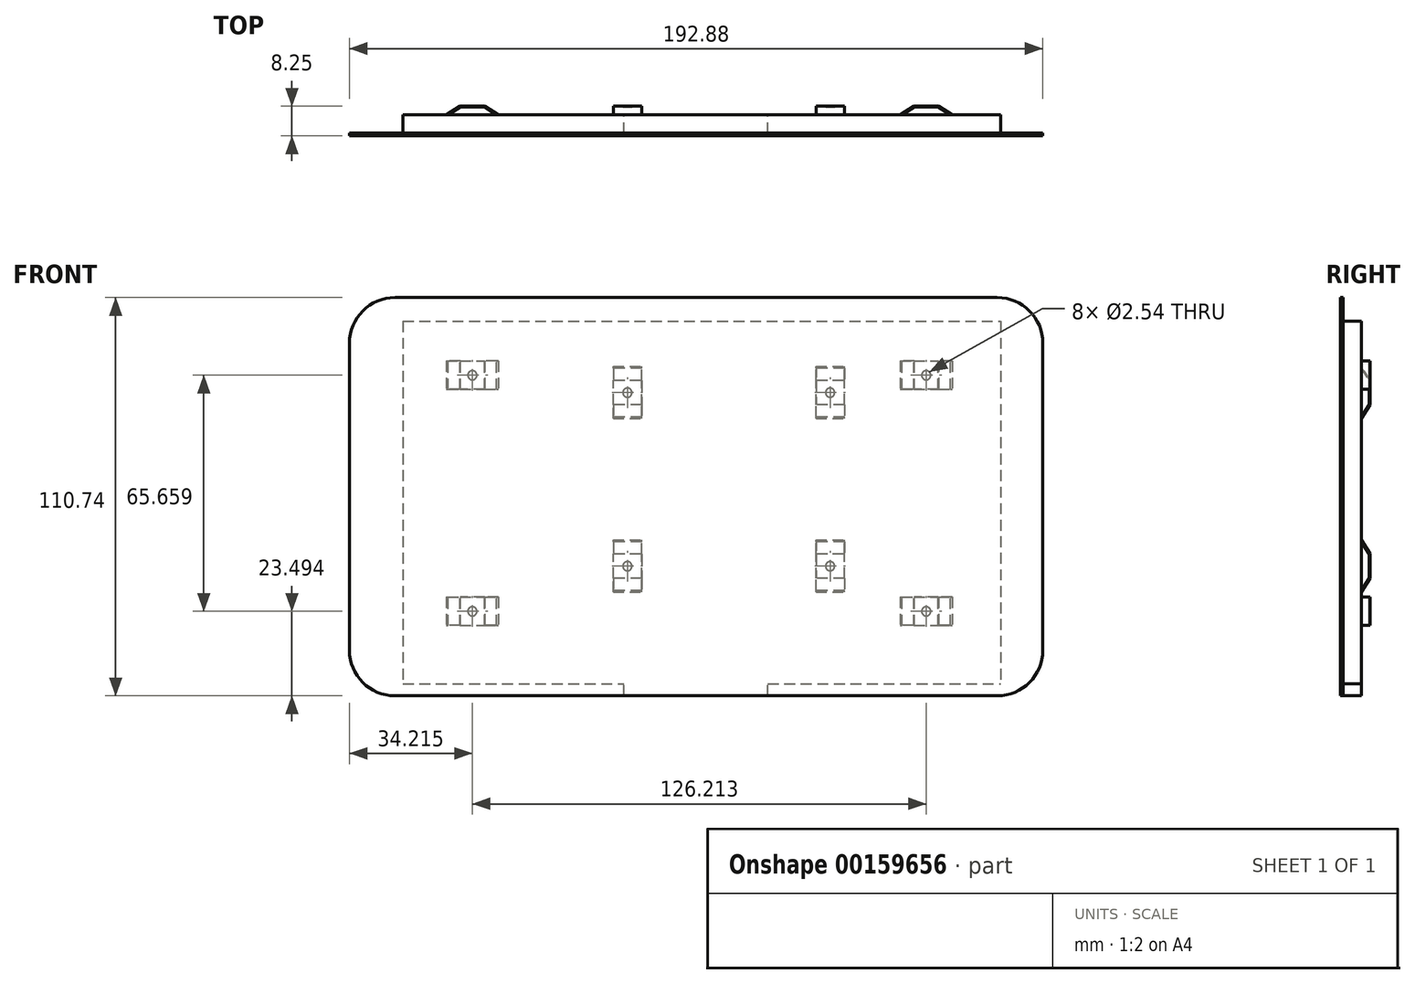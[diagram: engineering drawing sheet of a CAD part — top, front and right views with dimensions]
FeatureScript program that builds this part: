
annotation { "Feature Type Name" : "Feature", "Feature Type Description" : "" }
export const myFeature = defineFeature(function(context is Context, id is Id, definition is map)
    precondition{}
    {
        {
            var Q0;
            Q0=qCreatedBy(makeId("Front.planeOp"),FACE);
            var sketch = newSketch(context, id + "F0", { "sketchPlane" : qUnion([Q0])});
            skLineSegment(sketch, "E0.bottom", {"start": v(83.74, 55.37) * mm, "end": v(-83.74, 55.37) * mm});
            skLineSegment(sketch, "E0.top", {"start": v(83.74, -55.37) * mm, "end": v(-83.74, -55.37) * mm});
            skLineSegment(sketch, "E0.left", {"start": v(96.44, 42.67) * mm, "end": v(96.44, -42.67) * mm});
            skLineSegment(sketch, "E0.right", {"start": v(-96.44, 42.67) * mm, "end": v(-96.44, -42.67) * mm});
            skPoint(sketch, "E0.middle", {"position": v(0, 0) * mm});
            skPoint(sketch, "E1.visualSharp", {"position": v(-96.44, 55.37) * mm});
            skArc(sketch, "E1.filletArc", {"start": v(-83.74, 55.37) * mm, "mid": v(-92.72, 51.65) * mm, "end": v(-96.44, 42.67) * mm});
            skPoint(sketch, "E2.visualSharp", {"position": v(-96.44, -55.37) * mm});
            skArc(sketch, "E2.filletArc", {"start": v(-96.44, -42.67) * mm, "mid": v(-92.72, -51.65) * mm, "end": v(-83.74, -55.37) * mm});
            skPoint(sketch, "E3.visualSharp", {"position": v(96.44, -55.37) * mm});
            skArc(sketch, "E3.filletArc", {"start": v(83.74, -55.37) * mm, "mid": v(92.72, -51.65) * mm, "end": v(96.44, -42.67) * mm});
            skPoint(sketch, "E4.visualSharp", {"position": v(96.44, 55.37) * mm});
            skArc(sketch, "E4.filletArc", {"start": v(96.44, 42.67) * mm, "mid": v(92.72, 51.65) * mm, "end": v(83.74, 55.37) * mm});
            skSolve(sketch);
        }
        {
            var Q0;
            Q0 = qSketchRegion(id + "F0", true);
            extrude(context, id + "F1", {"entities" : qUnion([Q0]), "depth" : 0.76 * mm});
        }
        {
            var Q0;
            Q0=makeQuery(id+"F1.opExtrude","CAP_FACE",FACE,{"disambiguationData":[OSD([sQuery(id+"F0.wireOp",EDGE,"E0.bottom"),sQuery(id+"F0.wireOp",EDGE,"E0.top"),sQuery(id+"F0.wireOp",EDGE,"E0.left"),sQuery(id+"F0.wireOp",EDGE,"E0.right"),sQuery(id+"F0.wireOp",EDGE,"E1.filletArc"),sQuery(id+"F0.wireOp",EDGE,"E2.filletArc"),sQuery(id+"F0.wireOp",EDGE,"E3.filletArc"),sQuery(id+"F0.wireOp",EDGE,"E4.filletArc")])],"isStart":true});
            var sketch = newSketch(context, id + "F2", { "sketchPlane" : qUnion([Q0])});
            skLineSegment(sketch, "E5.bottom", {"start": v(81.54, 48.77) * mm, "end": v(-84.75, 48.77) * mm});
            skLineSegment(sketch, "E5.top", {"start": v(81.54, -52.03) * mm, "end": v(-84.75, -52.03) * mm});
            skLineSegment(sketch, "E5.left", {"start": v(81.54, 48.77) * mm, "end": v(81.54, -52.03) * mm});
            skLineSegment(sketch, "E5.right", {"start": v(-84.75, 48.77) * mm, "end": v(-84.75, -52.03) * mm});
            skPoint(sketch, "E5.middle", {"position": v(-1.6, -1.63) * mm});
            skSolve(sketch);
        }
        {
            var Q0;
            Q0 = qSketchRegion(id + "F2", true);
            extrude(context, id + "F3", {"entities" : qUnion([Q0]), "operationType" : NewBodyOperationType.ADD, "depth" : 5.08 * mm});
        }
        {
            var Q0;
            Q0=makeQuery(id+"F3.opExtrude","CAP_FACE",FACE,{"disambiguationData":[OSD([sQuery(id+"F2.wireOp",EDGE,"E5.bottom"),sQuery(id+"F2.wireOp",EDGE,"E5.top"),sQuery(id+"F2.wireOp",EDGE,"E5.left"),sQuery(id+"F2.wireOp",EDGE,"E5.right")])],"isStart":false});
            var sketch = newSketch(context, id + "F4", { "sketchPlane" : qUnion([Q0])});
            skLineSegment(sketch, "E6.bottom", {"start": v(-56.75, 37.72) * mm, "end": v(-71.23, 37.72) * mm});
            skLineSegment(sketch, "E6.top", {"start": v(-56.75, 29.85) * mm, "end": v(-71.23, 29.85) * mm});
            skLineSegment(sketch, "E6.left", {"start": v(-56.75, 37.72) * mm, "end": v(-56.75, 29.85) * mm});
            skLineSegment(sketch, "E6.right", {"start": v(-71.23, 37.72) * mm, "end": v(-71.23, 29.85) * mm});
            skPoint(sketch, "E6.middle", {"position": v(-63.99, 33.78) * mm});
            skLineSegment(sketch, "E7.bottom", {"start": v(-56.75, -27.94) * mm, "end": v(-71.23, -27.94) * mm});
            skLineSegment(sketch, "E7.top", {"start": v(-56.75, -35.81) * mm, "end": v(-71.23, -35.81) * mm});
            skLineSegment(sketch, "E7.left", {"start": v(-56.75, -27.94) * mm, "end": v(-56.75, -35.81) * mm});
            skLineSegment(sketch, "E7.right", {"start": v(-71.23, -27.94) * mm, "end": v(-71.23, -35.81) * mm});
            skPoint(sketch, "E7.middle", {"position": v(-63.99, -31.88) * mm});
            skLineSegment(sketch, "E8.bottom", {"start": v(69.46, 37.72) * mm, "end": v(54.99, 37.72) * mm});
            skLineSegment(sketch, "E8.top", {"start": v(69.46, 29.85) * mm, "end": v(54.99, 29.85) * mm});
            skLineSegment(sketch, "E8.left", {"start": v(69.46, 37.72) * mm, "end": v(69.46, 29.85) * mm});
            skLineSegment(sketch, "E8.right", {"start": v(54.99, 37.72) * mm, "end": v(54.99, 29.85) * mm});
            skPoint(sketch, "E8.middle", {"position": v(62.22, 33.78) * mm});
            skLineSegment(sketch, "E9.bottom", {"start": v(69.46, -27.94) * mm, "end": v(54.99, -27.94) * mm});
            skLineSegment(sketch, "E9.top", {"start": v(69.46, -35.81) * mm, "end": v(54.99, -35.81) * mm});
            skLineSegment(sketch, "E9.left", {"start": v(69.46, -27.94) * mm, "end": v(69.46, -35.81) * mm});
            skLineSegment(sketch, "E9.right", {"start": v(54.99, -27.94) * mm, "end": v(54.99, -35.81) * mm});
            skPoint(sketch, "E9.middle", {"position": v(62.22, -31.88) * mm});
            skLineSegment(sketch, "E10.bottom", {"start": v(-33.33, 21.72) * mm, "end": v(-41.2, 21.72) * mm});
            skLineSegment(sketch, "E10.top", {"start": v(-33.33, 36.2) * mm, "end": v(-41.2, 36.2) * mm});
            skLineSegment(sketch, "E10.left", {"start": v(-33.33, 21.72) * mm, "end": v(-33.33, 36.2) * mm});
            skLineSegment(sketch, "E10.right", {"start": v(-41.2, 21.72) * mm, "end": v(-41.2, 36.2) * mm});
            skPoint(sketch, "E10.middle", {"position": v(-37.27, 28.95) * mm});
            skLineSegment(sketch, "E11.bottom", {"start": v(23.04, 21.72) * mm, "end": v(15.17, 21.72) * mm});
            skLineSegment(sketch, "E11.top", {"start": v(23.04, 36.2) * mm, "end": v(15.17, 36.2) * mm});
            skLineSegment(sketch, "E11.left", {"start": v(23.04, 21.72) * mm, "end": v(23.04, 36.2) * mm});
            skLineSegment(sketch, "E11.right", {"start": v(15.17, 21.72) * mm, "end": v(15.17, 36.2) * mm});
            skPoint(sketch, "E11.middle", {"position": v(19.1, 28.95) * mm});
            skLineSegment(sketch, "E12.bottom", {"start": v(-33.33, -26.54) * mm, "end": v(-41.2, -26.54) * mm});
            skLineSegment(sketch, "E12.top", {"start": v(-33.33, -12.07) * mm, "end": v(-41.2, -12.07) * mm});
            skLineSegment(sketch, "E12.left", {"start": v(-33.33, -26.54) * mm, "end": v(-33.33, -12.07) * mm});
            skLineSegment(sketch, "E12.right", {"start": v(-41.2, -26.54) * mm, "end": v(-41.2, -12.07) * mm});
            skPoint(sketch, "E12.middle", {"position": v(-37.27, -19.3) * mm});
            skLineSegment(sketch, "E13.bottom", {"start": v(23.04, -26.54) * mm, "end": v(15.17, -26.54) * mm});
            skLineSegment(sketch, "E13.top", {"start": v(23.04, -12.07) * mm, "end": v(15.17, -12.07) * mm});
            skLineSegment(sketch, "E13.left", {"start": v(23.04, -26.54) * mm, "end": v(23.04, -12.07) * mm});
            skLineSegment(sketch, "E13.right", {"start": v(15.17, -26.54) * mm, "end": v(15.17, -12.07) * mm});
            skPoint(sketch, "E13.middle", {"position": v(19.1, -19.3) * mm});
            skLineSegment(sketch, "E14.bottom", {"start": v(-63.99, 33.78) * mm, "end": v(62.22, 33.78) * mm, "construction": true});
            skLineSegment(sketch, "E14.top", {"start": v(-63.99, -31.88) * mm, "end": v(62.22, -31.88) * mm, "construction": true});
            skLineSegment(sketch, "E14.left", {"start": v(-63.99, 33.78) * mm, "end": v(-63.99, -31.88) * mm, "construction": true});
            skLineSegment(sketch, "E14.right", {"start": v(62.22, 33.78) * mm, "end": v(62.22, -31.88) * mm, "construction": true});
            skLineSegment(sketch, "E15.bottom", {"start": v(-37.27, 28.95) * mm, "end": v(19.1, 28.95) * mm, "construction": true});
            skLineSegment(sketch, "E15.top", {"start": v(-37.27, -19.3) * mm, "end": v(19.1, -19.3) * mm, "construction": true});
            skLineSegment(sketch, "E15.left", {"start": v(-37.27, 28.95) * mm, "end": v(-37.27, -19.3) * mm, "construction": true});
            skLineSegment(sketch, "E15.right", {"start": v(19.1, 28.95) * mm, "end": v(19.1, -19.3) * mm, "construction": true});
            skCircle(sketch, "E16", {"center": v(-63.99, 33.78) * mm, "radius": 1.27 * mm});
            skCircle(sketch, "E17", {"center": v(62.22, 33.78) * mm, "radius": 1.27 * mm});
            skCircle(sketch, "E18", {"center": v(19.1, 28.95) * mm, "radius": 1.27 * mm});
            skCircle(sketch, "E19", {"center": v(-37.27, 28.95) * mm, "radius": 1.27 * mm});
            skCircle(sketch, "E20", {"center": v(-37.27, -19.3) * mm, "radius": 1.27 * mm});
            skCircle(sketch, "E21", {"center": v(19.1, -19.3) * mm, "radius": 1.27 * mm});
            skCircle(sketch, "E22", {"center": v(62.22, -31.88) * mm, "radius": 1.27 * mm});
            skCircle(sketch, "E23", {"center": v(-63.99, -31.88) * mm, "radius": 1.27 * mm});
            skSolve(sketch);
        }
        {
            var Q0;
            Q0 = qSketchRegion(id + "F4", true);
            extrude(context, id + "F5", {"entities" : qUnion([Q0]), "operationType" : NewBodyOperationType.ADD, "depth" : 2.41 * mm});
        }
        {
            var Q0;
            Q0=makeQuery(id+"F5.opExtrude","CAP_EDGE",EDGE,{"disambiguationData":[OSD([sQuery(id+"F4.wireOp",EDGE,"E6.left")])],"isStart":false});
            var Q1;
            Q1=makeQuery(id+"F5.opExtrude","CAP_EDGE",EDGE,{"disambiguationData":[OSD([sQuery(id+"F4.wireOp",EDGE,"E7.left")])],"isStart":false});
            var Q2;
            Q2=makeQuery(id+"F5.opExtrude","CAP_EDGE",EDGE,{"disambiguationData":[OSD([sQuery(id+"F4.wireOp",EDGE,"E12.bottom")])],"isStart":false});
            var Q3;
            Q3=makeQuery(id+"F5.opExtrude","CAP_EDGE",EDGE,{"disambiguationData":[OSD([sQuery(id+"F4.wireOp",EDGE,"E10.bottom")])],"isStart":false});
            var Q4;
            Q4=makeQuery(id+"F5.opExtrude","CAP_EDGE",EDGE,{"disambiguationData":[OSD([sQuery(id+"F4.wireOp",EDGE,"E13.bottom")])],"isStart":false});
            var Q5;
            Q5=makeQuery(id+"F5.opExtrude","CAP_EDGE",EDGE,{"disambiguationData":[OSD([sQuery(id+"F4.wireOp",EDGE,"E11.bottom")])],"isStart":false});
            var Q6;
            Q6=makeQuery(id+"F5.opExtrude","CAP_EDGE",EDGE,{"disambiguationData":[OSD([sQuery(id+"F4.wireOp",EDGE,"E8.left")])],"isStart":false});
            var Q7;
            Q7=makeQuery(id+"F5.opExtrude","CAP_EDGE",EDGE,{"disambiguationData":[OSD([sQuery(id+"F4.wireOp",EDGE,"E9.left")])],"isStart":false});
            var Q8;
            Q8=makeQuery(id+"F5.opExtrude","CAP_EDGE",EDGE,{"disambiguationData":[OSD([sQuery(id+"F4.wireOp",EDGE,"E6.right")])],"isStart":false});
            chamfer(context, id + "F6", {"entities" : qUnion([Q0, Q1, Q2, Q3, Q4, Q5, Q6, Q7, Q8]), "chamferType" : ChamferType.TWO_OFFSETS, "width1" : 2.41 * mm, "oppositeDirection" : false, "width2" : 3.8 * mm, "tangentPropagation" : true});
        }
        {
            var Q0;
            Q0=makeQuery(id+"F5.opExtrude","CAP_EDGE",EDGE,{"disambiguationData":[OSD([sQuery(id+"F4.wireOp",EDGE,"E10.top")])],"isStart":false});
            var Q1;
            Q1=makeQuery(id+"F5.opExtrude","CAP_EDGE",EDGE,{"disambiguationData":[OSD([sQuery(id+"F4.wireOp",EDGE,"E7.right")])],"isStart":false});
            var Q2;
            Q2=makeQuery(id+"F5.opExtrude","CAP_EDGE",EDGE,{"disambiguationData":[OSD([sQuery(id+"F4.wireOp",EDGE,"E12.top")])],"isStart":false});
            var Q3;
            Q3=makeQuery(id+"F5.opExtrude","CAP_EDGE",EDGE,{"disambiguationData":[OSD([sQuery(id+"F4.wireOp",EDGE,"E13.top")])],"isStart":false});
            var Q4;
            Q4=makeQuery(id+"F5.opExtrude","CAP_EDGE",EDGE,{"disambiguationData":[OSD([sQuery(id+"F4.wireOp",EDGE,"E11.top")])],"isStart":false});
            var Q5;
            Q5=makeQuery(id+"F5.opExtrude","CAP_EDGE",EDGE,{"disambiguationData":[OSD([sQuery(id+"F4.wireOp",EDGE,"E8.right")])],"isStart":false});
            var Q6;
            Q6=makeQuery(id+"F5.opExtrude","CAP_EDGE",EDGE,{"disambiguationData":[OSD([sQuery(id+"F4.wireOp",EDGE,"E9.right")])],"isStart":false});
            chamfer(context, id + "F7", {"entities" : qUnion([Q0, Q1, Q2, Q3, Q4, Q5, Q6]), "chamferType" : ChamferType.TWO_OFFSETS, "width1" : 2.41 * mm, "oppositeDirection" : true, "width2" : 3.8 * mm, "tangentPropagation" : true});
        }
        {
            var Q0;
            Q0=makeQuery(id+"F5.opExtrude","SWEPT_FACE",FACE,{"disambiguationData":[OSD([sQuery(id+"F4.wireOp",EDGE,"E8.bottom")])]});
            var sketch = newSketch(context, id + "F8", { "sketchPlane" : qUnion([Q0])});
            skLineSegment(sketch, "E24.0", {"start": v(-68.99, 5.08) * mm, "end": v(-55.46, 5.08) * mm});
            skLineSegment(sketch, "E25.0", {"start": v(57.22, 5.08) * mm, "end": v(70.75, 5.08) * mm});
            skLineSegment(sketch, "E26.0", {"start": v(-65.58, 7.24) * mm, "end": v(-68.99, 5.08) * mm});
            skLineSegment(sketch, "E26.1", {"start": v(-65.58, 7.24) * mm, "end": v(-58.87, 7.24) * mm});
            skLineSegment(sketch, "E26.2", {"start": v(-55.46, 5.08) * mm, "end": v(-58.87, 7.24) * mm});
            skLineSegment(sketch, "E27.0", {"start": v(60.63, 7.24) * mm, "end": v(57.22, 5.08) * mm});
            skLineSegment(sketch, "E27.1", {"start": v(60.63, 7.24) * mm, "end": v(67.34, 7.24) * mm});
            skLineSegment(sketch, "E27.2", {"start": v(70.75, 5.08) * mm, "end": v(67.34, 7.24) * mm});
            skPoint(sketch, "E28.orphan", {"position": v(56.75, 5.08) * mm});
            skPoint(sketch, "E29.orphan", {"position": v(71.23, 5.08) * mm});
            skPoint(sketch, "E30.orphan", {"position": v(-54.99, 5.08) * mm});
            skPoint(sketch, "E31.orphan", {"position": v(-69.46, 5.08) * mm});
            skSolve(sketch);
        }
        {
            var Q0;
            Q0 = qSketchRegion(id + "F8", true);
            var Q1;
            Q1=makeQuery(id+"F5.opExtrude","SWEPT_FACE",FACE,{"disambiguationData":[OSD([sQuery(id+"F4.wireOp",EDGE,"E9.top")])]});
            extrude(context, id + "F9", {"entities" : qUnion([Q0]), "operationType" : NewBodyOperationType.REMOVE, "endBound" : BoundingType.UP_TO_SURFACE, "oppositeDirection" : true, "endBoundEntityFace" : qUnion([Q1]), "depth" : 25.4 * mm});
        }
        {
            var Q0;
            Q0=makeQuery(id+"F5.opExtrude","SWEPT_FACE",FACE,{"disambiguationData":[OSD([sQuery(id+"F4.wireOp",EDGE,"E11.left")])]});
            var sketch = newSketch(context, id + "F10", { "sketchPlane" : qUnion([Q0])});
            skLineSegment(sketch, "E32.0", {"start": v(-5.08, -26.07) * mm, "end": v(-5.08, -12.54) * mm});
            skLineSegment(sketch, "E33.0", {"start": v(-5.08, 22.2) * mm, "end": v(-5.08, 35.72) * mm});
            skLineSegment(sketch, "E34.0", {"start": v(-7.24, -22.66) * mm, "end": v(-5.08, -26.07) * mm});
            skLineSegment(sketch, "E34.1", {"start": v(-7.24, -22.66) * mm, "end": v(-7.24, -15.95) * mm});
            skLineSegment(sketch, "E34.2", {"start": v(-5.08, -12.54) * mm, "end": v(-7.24, -15.95) * mm});
            skLineSegment(sketch, "E35.0", {"start": v(-7.24, 25.6) * mm, "end": v(-5.08, 22.2) * mm});
            skLineSegment(sketch, "E35.1", {"start": v(-7.24, 25.6) * mm, "end": v(-7.24, 32.31) * mm});
            skLineSegment(sketch, "E35.2", {"start": v(-5.08, 35.72) * mm, "end": v(-7.24, 32.31) * mm});
            skPoint(sketch, "E36.orphan", {"position": v(-5.08, -12.07) * mm});
            skPoint(sketch, "E37.orphan", {"position": v(-5.08, -26.54) * mm});
            skPoint(sketch, "E38.orphan", {"position": v(-5.08, 21.72) * mm});
            skPoint(sketch, "E39.orphan", {"position": v(-5.08, 36.2) * mm});
            skSolve(sketch);
        }
        {
            var Q0;
            Q0 = qSketchRegion(id + "F10", true);
            var Q1;
            Q1=makeQuery(id+"F5.opExtrude","SWEPT_FACE",FACE,{"disambiguationData":[OSD([sQuery(id+"F4.wireOp",EDGE,"E12.right")])]});
            extrude(context, id + "F11", {"entities" : qUnion([Q0]), "operationType" : NewBodyOperationType.REMOVE, "endBound" : BoundingType.UP_TO_SURFACE, "oppositeDirection" : true, "endBoundEntityFace" : qUnion([Q1]), "depth" : 25.4 * mm});
        }
        {
            var Q0;
            Q0=makeQuery(id+"F3.opExtrude","SWEPT_FACE",FACE,{"disambiguationData":[OSD([sQuery(id+"F2.wireOp",EDGE,"E5.top")])]});
            var sketch = newSketch(context, id + "F12", { "sketchPlane" : qUnion([Q0])});
            skLineSegment(sketch, "E40.bottom", {"start": v(19.93, 0) * mm, "end": v(-20.07, 0) * mm});
            skLineSegment(sketch, "E40.top", {"start": v(19.93, -5.08) * mm, "end": v(-20.07, -5.08) * mm});
            skLineSegment(sketch, "E40.left", {"start": v(19.93, 0) * mm, "end": v(19.93, -5.08) * mm});
            skLineSegment(sketch, "E40.right", {"start": v(-20.07, 0) * mm, "end": v(-20.07, -5.08) * mm});
            skSolve(sketch);
        }
        {
            var Q0;
            Q0 = qSketchRegion(id + "F12", true);
            var Q1;
            Q1=makeQuery(id+"F1.opExtrude","SWEPT_FACE",FACE,{"disambiguationData":[OSD([sQuery(id+"F0.wireOp",EDGE,"E0.top")])]});
            extrude(context, id + "F13", {"entities" : qUnion([Q0]), "operationType" : NewBodyOperationType.ADD, "endBound" : BoundingType.UP_TO_SURFACE, "endBoundEntityFace" : qUnion([Q1]), "depth" : 25.4 * mm});
        }
    });
